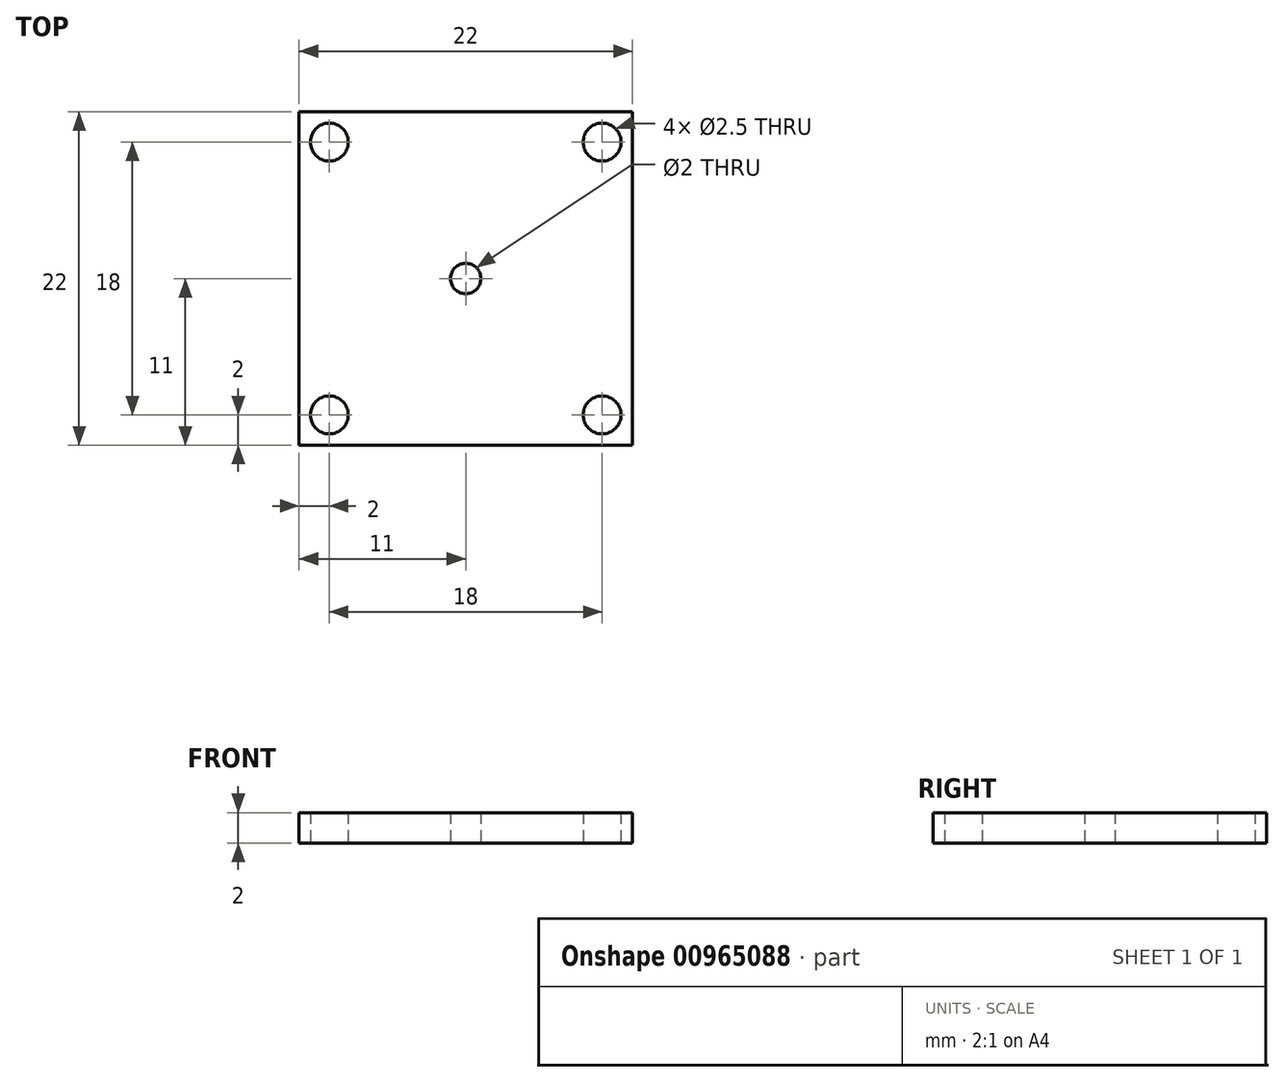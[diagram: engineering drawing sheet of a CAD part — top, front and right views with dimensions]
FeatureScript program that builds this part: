
annotation { "Feature Type Name" : "Feature", "Feature Type Description" : "" }
export const myFeature = defineFeature(function(context is Context, id is Id, definition is map)
    precondition{}
    {
        {
            var Q0;
            Q0=qCreatedBy(makeId("Top.planeOp"),FACE);
            var sketch = newSketch(context, id + "F0", { "sketchPlane" : qUnion([Q0])});
            skLineSegment(sketch, "E0.bottom", {"start": v(0, 0) * mm, "end": v(22, 0) * mm});
            skLineSegment(sketch, "E0.top", {"start": v(0, 22) * mm, "end": v(22, 22) * mm});
            skLineSegment(sketch, "E0.left", {"start": v(0, 0) * mm, "end": v(0, 22) * mm});
            skLineSegment(sketch, "E0.right", {"start": v(22, 0) * mm, "end": v(22, 22) * mm});
            skCircle(sketch, "E1", {"center": v(11, 11) * mm, "radius": 1 * mm});
            skCircle(sketch, "E2", {"center": v(20, 20) * mm, "radius": 1.25 * mm});
            skCircle(sketch, "E3", {"center": v(2, 20) * mm, "radius": 1.25 * mm});
            skCircle(sketch, "E4", {"center": v(2, 2) * mm, "radius": 1.25 * mm});
            skCircle(sketch, "E5", {"center": v(20, 2) * mm, "radius": 1.25 * mm});
            skSolve(sketch);
        }
        {
            var Q0;
            Q0=makeQuery(id+"F0.imprint","IMPRINT",FACE,{"disambiguationData":[TD([[makeQuery(id+"F0.imprint","IMPRINT",EDGE,{"derivedFrom":sQuery(id+"F0.wireOp",EDGE,"E0.bottom")}),1.0]])]});
            extrude(context, id + "F1", {"entities" : qUnion([Q0]), "depth" : 2 * mm, "offsetDistance" : 25 * mm});
        }
    });
